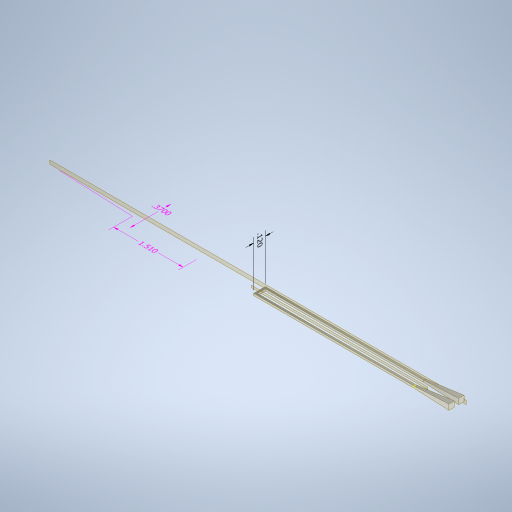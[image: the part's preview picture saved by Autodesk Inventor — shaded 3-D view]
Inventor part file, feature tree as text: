
AUTODESK INVENTOR PART (.ipt)
format: ipt  version: 2024.2 (Build 282272000, 272)  size: 314,368 bytes
history: native  units: in
note: dims shown in document units (in); Inventor stores cm internally (conversion verified against a paired STEP export)
features: other x5, plane x4, sketch x4, sweep x1, loft x1, mirror x1, projected_geometry x1
ambient origin geometry x8: Origin, YZ Plane, XZ Plane, XY Plane, X Axis, Y Axis, Z Axis, Center Point
bodies: Solid1 (feature_tree)
feature tree (17):
  other  "Annotations"
  sweep  "Sweep1"
  plane  "Work Plane1"
  plane  "Work Plane2"
  plane  "Work Plane4"
  sketch  "Sketch15"  dims[d86=-0.1175in]
  sketch  "Sketch16"  dims[d89=0.1in d90=0.0in d91=0.0in d92=0.0in d98=0.02in d99=0.02in d100=0.055in d102=0.055in d104=0.0in d109=0.0in d110=90.0deg d111=0.0in d112=90.0deg d116=-0.06in d113=0.0in d114=0.3937in d115=0.12in d42=0.2341in d43=0.169in d44=0.37in d48=0.2141in d49=0.2512in d50=1.51in]
  loft  "Loft3"
  plane  "Work Plane5"
  mirror  "Mirror3"
  sketch  "Sketch1"  dims[d6=0.0in d7=0.0in d11=0.375in d19=-0.25in]
  sketch  "Sketch2"  dims[d69=1.625in d70=1.625in]
  projected_geometry  "Projected Loop1"
  other  "Edges4"
  other  "Linear Dimension 1"
  other  "Linear Dimension 3"
  other  "Linear Dimension 4"
